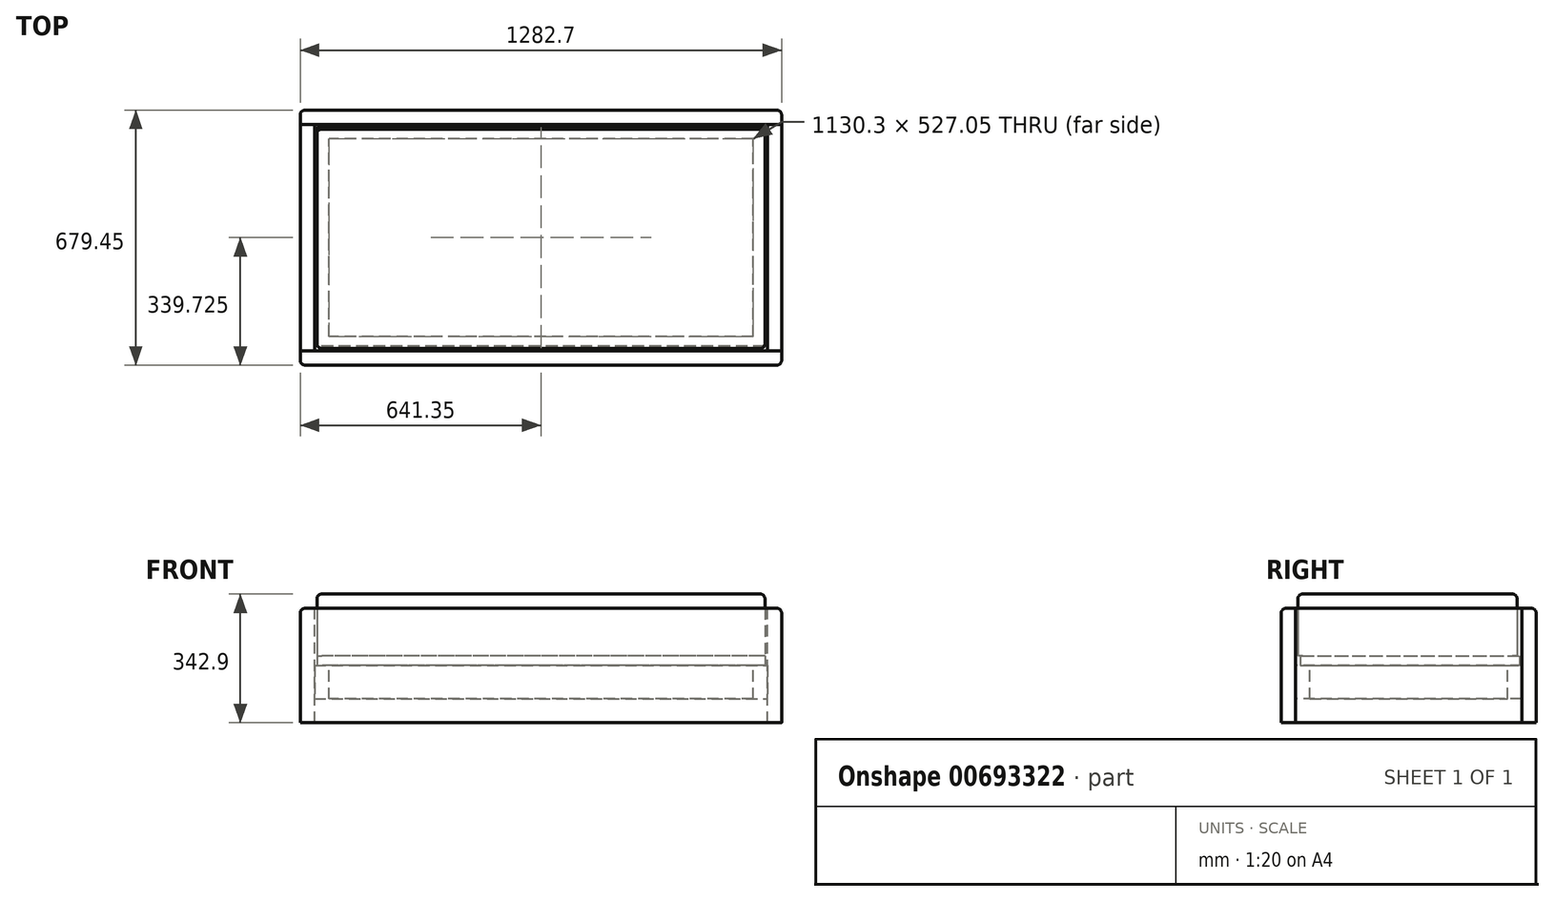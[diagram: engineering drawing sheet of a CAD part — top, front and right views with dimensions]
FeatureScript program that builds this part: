
annotation { "Feature Type Name" : "Feature", "Feature Type Description" : "" }
export const myFeature = defineFeature(function(context is Context, id is Id, definition is map)
    precondition{}
    {
        {
            var Q0;
            Q0=qCreatedBy(makeId("Front.planeOp"),FACE);
            var sketch = newSketch(context, id + "F0", { "sketchPlane" : qUnion([Q0])});
            skLineSegment(sketch, "E0.bottom", {"start": v(0, 0) * mm, "end": v(1282.7, 0) * mm});
            skLineSegment(sketch, "E0.top", {"start": v(0, 304.8) * mm, "end": v(1282.7, 304.8) * mm});
            skLineSegment(sketch, "E0.left", {"start": v(0, 0) * mm, "end": v(0, 304.8) * mm});
            skLineSegment(sketch, "E0.right", {"start": v(1282.7, 0) * mm, "end": v(1282.7, 304.8) * mm});
            skSolve(sketch);
        }
        {
            var Q0;
            Q0 = qSketchRegion(id + "F0", true);
            extrude(context, id + "F1", {"entities" : qUnion([Q0]), "depth" : 38.1 * mm, "offsetDistance" : 25.4 * mm});
        }
        {
            var Q0;
            Q0=makeQuery(id+"F1.opExtrude","CAP_FACE",FACE,{"disambiguationData":[OSD([sQuery(id+"F0.wireOp",EDGE,"E0.bottom"),sQuery(id+"F0.wireOp",EDGE,"E0.top"),sQuery(id+"F0.wireOp",EDGE,"E0.left"),sQuery(id+"F0.wireOp",EDGE,"E0.right")])],"isStart":true});
            var sketch = newSketch(context, id + "F2", { "sketchPlane" : qUnion([Q0])});
            skLineSegment(sketch, "E1.bottom", {"start": v(-1282.7, 0) * mm, "end": v(-1244.6, 0) * mm});
            skLineSegment(sketch, "E1.top", {"start": v(-1282.7, 304.8) * mm, "end": v(-1244.6, 304.8) * mm});
            skLineSegment(sketch, "E1.left", {"start": v(-1282.7, 0) * mm, "end": v(-1282.7, 304.8) * mm});
            skLineSegment(sketch, "E1.right", {"start": v(-1244.6, 0) * mm, "end": v(-1244.6, 304.8) * mm});
            skLineSegment(sketch, "E2.bottom", {"start": v(0, 0) * mm, "end": v(-38.1, 0) * mm});
            skLineSegment(sketch, "E2.top", {"start": v(0, 304.8) * mm, "end": v(-38.1, 304.8) * mm});
            skLineSegment(sketch, "E2.left", {"start": v(0, 0) * mm, "end": v(0, 304.8) * mm});
            skLineSegment(sketch, "E2.right", {"start": v(-38.1, 0) * mm, "end": v(-38.1, 304.8) * mm});
            skSolve(sketch);
        }
        {
            var Q0;
            Q0 = qSketchRegion(id + "F2", true);
            extrude(context, id + "F3", {"entities" : qUnion([Q0]), "depth" : 603.25 * mm, "offsetDistance" : 25.4 * mm});
        }
        {
            var Q0;
            Q0=makeQuery(id+"F3.opExtrude","SWEPT_FACE",FACE,{"disambiguationData":[OSD([sQuery(id+"F2.wireOp",EDGE,"E2.left")])]});
            var sketch = newSketch(context, id + "F4", { "sketchPlane" : qUnion([Q0])});
            skLineSegment(sketch, "E3.bottom", {"start": v(-603.25, 0) * mm, "end": v(-641.35, 0) * mm});
            skLineSegment(sketch, "E3.top", {"start": v(-603.25, 304.8) * mm, "end": v(-641.35, 304.8) * mm});
            skLineSegment(sketch, "E3.left", {"start": v(-603.25, 0) * mm, "end": v(-603.25, 304.8) * mm});
            skLineSegment(sketch, "E3.right", {"start": v(-641.35, 0) * mm, "end": v(-641.35, 304.8) * mm});
            skSolve(sketch);
        }
        {
            var Q0;
            Q0 = qSketchRegion(id + "F4", true);
            var Q1;
            Q1=makeQuery(id+"F3.opExtrude","SWEPT_FACE",FACE,{"disambiguationData":[OSD([sQuery(id+"F2.wireOp",EDGE,"E1.left")])]});
            extrude(context, id + "F5", {"entities" : qUnion([Q0]), "endBound" : BoundingType.UP_TO_SURFACE, "oppositeDirection" : true, "depth" : 1092.2 * mm, "endBoundEntityFace" : qUnion([Q1]), "offsetDistance" : 25.4 * mm});
        }
        {
            var Q0;
            Q0=makeQuery(id+"F1.opExtrude","CAP_FACE",FACE,{"disambiguationData":[OSD([sQuery(id+"F0.wireOp",EDGE,"E0.bottom"),sQuery(id+"F0.wireOp",EDGE,"E0.top"),sQuery(id+"F0.wireOp",EDGE,"E0.left"),sQuery(id+"F0.wireOp",EDGE,"E0.right")])],"isStart":true});
            var sketch = newSketch(context, id + "F6", { "sketchPlane" : qUnion([Q0])});
            skLineSegment(sketch, "E4.bottom", {"start": v(-1244.6, 63.5) * mm, "end": v(-38.1, 63.5) * mm});
            skLineSegment(sketch, "E4.top", {"start": v(-1244.6, 152.4) * mm, "end": v(-38.1, 152.4) * mm});
            skLineSegment(sketch, "E4.left", {"start": v(-1244.6, 63.5) * mm, "end": v(-1244.6, 152.4) * mm});
            skLineSegment(sketch, "E4.right", {"start": v(-38.1, 63.5) * mm, "end": v(-38.1, 152.4) * mm});
            skSolve(sketch);
        }
        {
            var Q0;
            Q0 = qSketchRegion(id + "F6", true);
            extrude(context, id + "F7", {"entities" : qUnion([Q0]), "endBound" : BoundingType.UP_TO_NEXT, "depth" : 25.4 * mm, "offsetDistance" : 25.4 * mm});
        }
        {
            var Q0;
            Q0=makeQuery(id+"F7.opExtrude","SWEPT_FACE",FACE,{"disambiguationData":[OSD([sQuery(id+"F6.wireOp",EDGE,"E4.top")])]});
            var sketch = newSketch(context, id + "F8", { "sketchPlane" : qUnion([Q0])});
            skLineSegment(sketch, "E5.bottom", {"start": v(1206.5, 38.1) * mm, "end": v(76.2, 38.1) * mm});
            skLineSegment(sketch, "E5.top", {"start": v(1206.5, 565.15) * mm, "end": v(76.2, 565.15) * mm});
            skLineSegment(sketch, "E5.left", {"start": v(1206.5, 38.1) * mm, "end": v(1206.5, 565.15) * mm});
            skLineSegment(sketch, "E5.right", {"start": v(76.2, 38.1) * mm, "end": v(76.2, 565.15) * mm});
            skSolve(sketch);
        }
        {
            var Q0;
            Q0 = qSketchRegion(id + "F8", true);
            extrude(context, id + "F9", {"entities" : qUnion([Q0]), "operationType" : NewBodyOperationType.REMOVE, "endBound" : BoundingType.THROUGH_ALL, "oppositeDirection" : true, "depth" : 25.4 * mm, "offsetDistance" : 25.4 * mm});
        }
        {
            var Q0;
            Q0=makeQuery(id+"F7.opExtrude","SWEPT_FACE",FACE,{"disambiguationData":[OSD([sQuery(id+"F6.wireOp",EDGE,"E4.top")])]});
            var sketch = newSketch(context, id + "F10", { "sketchPlane" : qUnion([Q0])});
            skLineSegment(sketch, "E6.bottom", {"start": v(1238.25, 12.7) * mm, "end": v(44.45, 12.7) * mm});
            skLineSegment(sketch, "E6.top", {"start": v(1238.25, 596.9) * mm, "end": v(44.45, 596.9) * mm});
            skLineSegment(sketch, "E6.left", {"start": v(1238.25, 12.7) * mm, "end": v(1238.25, 596.9) * mm});
            skLineSegment(sketch, "E6.right", {"start": v(44.45, 12.7) * mm, "end": v(44.45, 596.9) * mm});
            skSolve(sketch);
        }
        {
            var Q0;
            Q0 = qSketchRegion(id + "F10", true);
            extrude(context, id + "F11", {"entities" : qUnion([Q0]), "depth" : 25.4 * mm, "offsetDistance" : 25.4 * mm});
        }
        {
            var Q0;
            Q0=makeQuery(id+"F11.opExtrude","CAP_FACE",FACE,{"disambiguationData":[OSD([sQuery(id+"F10.wireOp",EDGE,"E6.bottom"),sQuery(id+"F10.wireOp",EDGE,"E6.top"),sQuery(id+"F10.wireOp",EDGE,"E6.left"),sQuery(id+"F10.wireOp",EDGE,"E6.right")])],"isStart":false});
            var sketch = newSketch(context, id + "F12", { "sketchPlane" : qUnion([Q0])});
            skLineSegment(sketch, "E7.bottom", {"start": v(1238.25, 6.35) * mm, "end": v(44.45, 6.35) * mm});
            skLineSegment(sketch, "E7.top", {"start": v(1238.25, 590.55) * mm, "end": v(44.45, 590.55) * mm});
            skLineSegment(sketch, "E7.left", {"start": v(1238.25, 6.35) * mm, "end": v(1238.25, 590.55) * mm});
            skLineSegment(sketch, "E7.right", {"start": v(44.45, 6.35) * mm, "end": v(44.45, 590.55) * mm});
            skSolve(sketch);
        }
        {
            var Q0;
            Q0 = qSketchRegion(id + "F12", true);
            extrude(context, id + "F13", {"entities" : qUnion([Q0]), "depth" : 165.1 * mm, "offsetDistance" : 25.4 * mm});
        }
        {
            var Q0;
            Q0=makeQuery(id+"F5.opExtrude","CAP_EDGE",EDGE,{"disambiguationData":[OSD([sQuery(id+"F4.wireOp",EDGE,"E3.right")])],"isStart":true});
            var Q1;
            Q1=makeQuery(id+"F5.opExtrude","CAP_EDGE",EDGE,{"disambiguationData":[OSD([sQuery(id+"F4.wireOp",EDGE,"E3.right")])],"isStart":false});
            var Q2;
            Q2=makeQuery(id+"F1.opExtrude","CAP_EDGE",EDGE,{"disambiguationData":[OSD([sQuery(id+"F0.wireOp",EDGE,"E0.left")])],"isStart":false});
            var Q3;
            Q3=makeQuery(id+"F1.opExtrude","CAP_EDGE",EDGE,{"disambiguationData":[OSD([sQuery(id+"F0.wireOp",EDGE,"E0.right")])],"isStart":false});
            fillet(context, id + "F14", {"entities" : qUnion([Q0, Q1, Q2, Q3]), "radius" : 12.7 * mm, "tangentPropagation" : true, "allowEdgeOverflow" : false});
        }
        {
            var Q0;
            Q0=makeQuery(id+"F5.opExtrude","SWEPT_EDGE",EDGE,{"disambiguationData":[OSD([sQuery(id+"F4.wireOp",EDGE,"E3.top"),sQuery(id+"F4.wireOp",EDGE,"E3.right")])]});
            var Q1;
            Q1=makeQuery(id+"F3.opExtrude","SWEPT_EDGE",EDGE,{"disambiguationData":[OSD([sQuery(id+"F2.wireOp",EDGE,"E2.top"),sQuery(id+"F2.wireOp",EDGE,"E2.left")])]});
            var Q2;
            Q2=makeQuery(id+"F3.opExtrude","SWEPT_EDGE",EDGE,{"disambiguationData":[OSD([sQuery(id+"F2.wireOp",EDGE,"E1.top"),sQuery(id+"F2.wireOp",EDGE,"E1.left")])]});
            var Q3;
            Q3=makeQuery(id+"F1.opExtrude","CAP_EDGE",EDGE,{"disambiguationData":[OSD([sQuery(id+"F0.wireOp",EDGE,"E0.top")])],"isStart":false});
            fillet(context, id + "F15", {"entities" : qUnion([Q0, Q1, Q2, Q3]), "radius" : 12.7 * mm, "tangentPropagation" : true, "allowEdgeOverflow" : false});
        }
        {
            var Q0;
            Q0=makeQuery(id+"F13.opExtrude","SWEPT_EDGE",EDGE,{"disambiguationData":[OSD([sQuery(id+"F10.wireOp",EDGE,"E6.right"),sQuery(id+"F12.wireOp",EDGE,"E7.top"),sQuery(id+"F12.wireOp",EDGE,"E7.right")])]});
            var Q1;
            Q1=makeQuery(id+"F13.opExtrude","SWEPT_EDGE",EDGE,{"disambiguationData":[OSD([sQuery(id+"F10.wireOp",EDGE,"E6.left"),sQuery(id+"F12.wireOp",EDGE,"E7.top"),sQuery(id+"F12.wireOp",EDGE,"E7.left")])]});
            var Q2;
            Q2=makeQuery(id+"F13.opExtrude","SWEPT_EDGE",EDGE,{"disambiguationData":[OSD([sQuery(id+"F12.wireOp",EDGE,"E7.bottom"),sQuery(id+"F12.wireOp",EDGE,"E7.left")])]});
            var Q3;
            Q3=makeQuery(id+"F13.opExtrude","SWEPT_EDGE",EDGE,{"disambiguationData":[OSD([sQuery(id+"F12.wireOp",EDGE,"E7.bottom"),sQuery(id+"F12.wireOp",EDGE,"E7.right")])]});
            fillet(context, id + "F16", {"entities" : qUnion([Q0, Q1, Q2, Q3]), "radius" : 12.7 * mm, "tangentPropagation" : true, "allowEdgeOverflow" : false});
        }
        {
            var Q0;
            Q0=makeQuery(id+"F13.opExtrude","CAP_EDGE",EDGE,{"disambiguationData":[OSD([sQuery(id+"F12.wireOp",EDGE,"E7.top")])],"isStart":false});
            fillet(context, id + "F17", {"entities" : qUnion([Q0]), "radius" : 12.7 * mm, "tangentPropagation" : true, "allowEdgeOverflow" : false});
        }
    });
